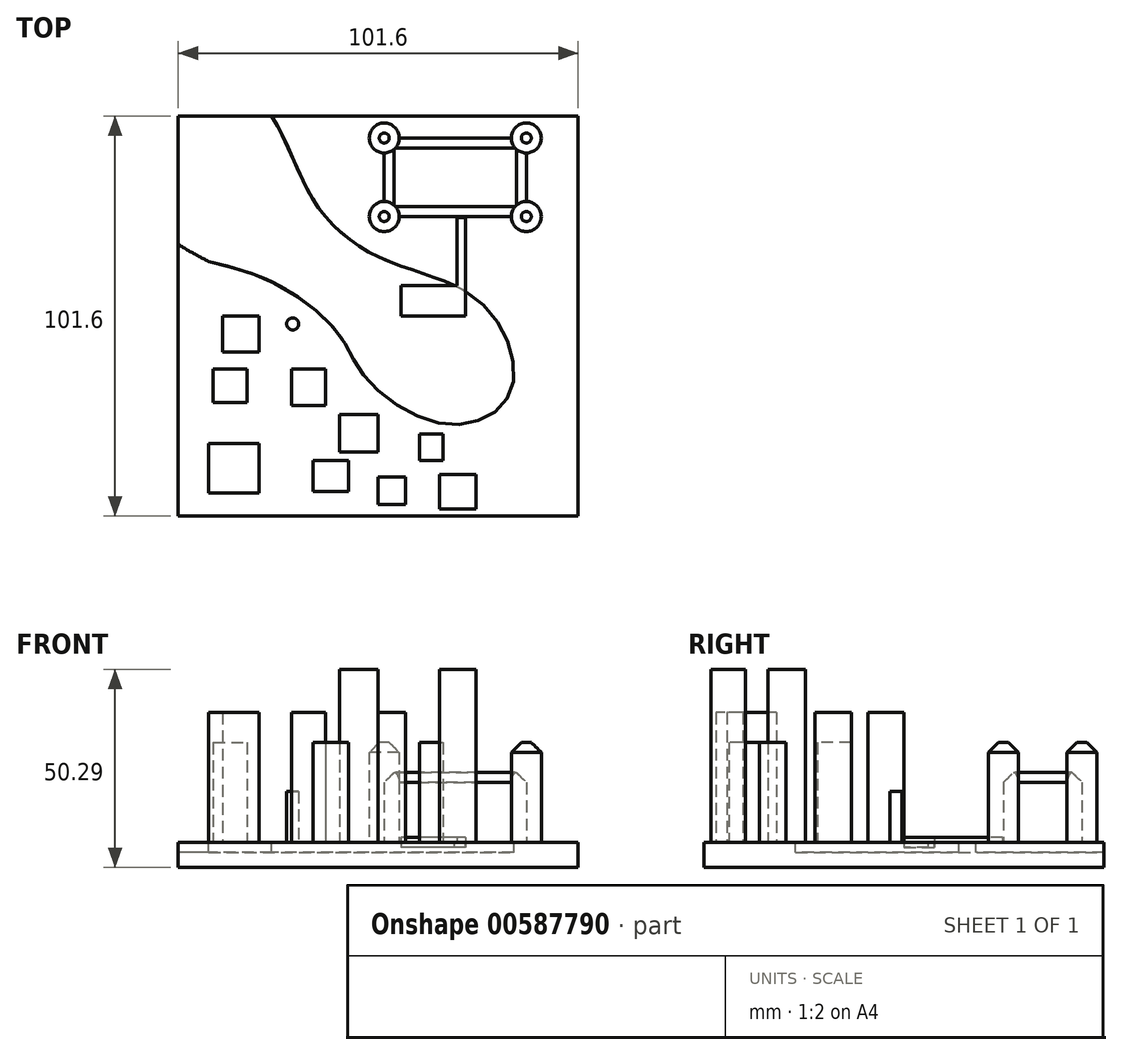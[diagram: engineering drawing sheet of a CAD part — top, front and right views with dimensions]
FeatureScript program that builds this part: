
annotation { "Feature Type Name" : "Feature", "Feature Type Description" : "" }
export const myFeature = defineFeature(function(context is Context, id is Id, definition is map)
    precondition{}
    {
        {
            var Q0;
            Q0=qCreatedBy(makeId("Top.planeOp"),FACE);
            var sketch = newSketch(context, id + "F0", { "sketchPlane" : qUnion([Q0])});
            skLineSegment(sketch, "E0.bottom", {"start": v(-50.8, -50.8) * mm, "end": v(50.8, -50.8) * mm});
            skLineSegment(sketch, "E0.top", {"start": v(-50.8, 50.8) * mm, "end": v(50.8, 50.8) * mm});
            skLineSegment(sketch, "E0.left", {"start": v(-50.8, -50.8) * mm, "end": v(-50.8, 50.8) * mm});
            skLineSegment(sketch, "E0.right", {"start": v(50.8, -50.8) * mm, "end": v(50.8, 50.8) * mm});
            skPoint(sketch, "E0.middle", {"position": v(0, 0) * mm});
            skSolve(sketch);
        }
        {
            var Q0;
            Q0 = qSketchRegion(id + "F0", true);
            extrude(context, id + "F1", {"entities" : qUnion([Q0]), "oppositeDirection" : true, "depth" : 6.35 * mm, "offsetDistance" : 25.4 * mm});
        }
        {
            var Q0;
            Q0=qCreatedBy(makeId("Top.planeOp"),FACE);
            var sketch = newSketch(context, id + "F2", { "sketchPlane" : qUnion([Q0])});
            skFitSpline(sketch, "E1", {"points": [v(-43.1, 13.89) * mm, v(-25.52, 7.95) * mm, v(-9.85, -4.87) * mm, v(-3.68, -15.08) * mm, v(10.8, -25.76) * mm, v(25.05, -26.7) * mm, v(33.6, -19.35) * mm, v(32.65, -5.82) * mm, v(21.72, 6.53) * mm, v(0, 15.08) * mm, v(-16.5, 29.56) * mm, v(-26.95, 50.69) * mm, v(-40.6, 65.37) * mm], "startDerivative": vector(201.87, -49.36) * mm, "endDerivative": vector(-139.7, 111.84) * mm});
            skFitSpline(sketch, "E2", {"points": [v(-43.1, 13.89) * mm, v(-58.29, 25.05) * mm, v(-64.82, 45.42) * mm], "startDerivative": vector(-35.32, 18.48) * mm, "endDerivative": vector(-0.32, 35.88) * mm});
            skLineSegment(sketch, "E3", {"start": v(-40.6, 65.37) * mm, "end": v(-64.82, 45.42) * mm});
            skSolve(sketch);
        }
        {
            var Q0;
            Q0 = qSketchRegion(id + "F2", true);
            extrude(context, id + "F3", {"entities" : qUnion([Q0]), "operationType" : NewBodyOperationType.REMOVE, "oppositeDirection" : true, "depth" : 2.54 * mm, "offsetDistance" : 25.4 * mm});
        }
        {
            var Q0;
            Q0=qCreatedBy(makeId("Top.planeOp"),FACE);
            var sketch = newSketch(context, id + "F4", { "sketchPlane" : qUnion([Q0])});
            skLineSegment(sketch, "E4.bottom", {"start": v(-41.9, -13.41) * mm, "end": v(-33.36, -13.41) * mm});
            skLineSegment(sketch, "E4.top", {"start": v(-41.9, -21.96) * mm, "end": v(-33.36, -21.96) * mm});
            skLineSegment(sketch, "E4.left", {"start": v(-41.9, -13.41) * mm, "end": v(-41.9, -21.96) * mm});
            skLineSegment(sketch, "E4.right", {"start": v(-33.36, -13.41) * mm, "end": v(-33.36, -21.96) * mm});
            skLineSegment(sketch, "E5.bottom", {"start": v(-16.5, -36.68) * mm, "end": v(-7.48, -36.68) * mm});
            skLineSegment(sketch, "E5.top", {"start": v(-16.5, -44.52) * mm, "end": v(-7.48, -44.52) * mm});
            skLineSegment(sketch, "E5.left", {"start": v(-16.5, -36.68) * mm, "end": v(-16.5, -44.52) * mm});
            skLineSegment(sketch, "E5.right", {"start": v(-7.48, -36.68) * mm, "end": v(-7.48, -44.52) * mm});
            skLineSegment(sketch, "E6.bottom", {"start": v(10.57, -30.03) * mm, "end": v(16.5, -30.03) * mm});
            skLineSegment(sketch, "E6.top", {"start": v(10.57, -36.68) * mm, "end": v(16.5, -36.68) * mm});
            skLineSegment(sketch, "E6.left", {"start": v(10.57, -30.03) * mm, "end": v(10.57, -36.68) * mm});
            skLineSegment(sketch, "E6.right", {"start": v(16.5, -30.03) * mm, "end": v(16.5, -36.68) * mm});
            skSolve(sketch);
        }
        {
            var Q0;
            Q0=qCreatedBy(makeId("Top.planeOp"),FACE);
            var sketch = newSketch(context, id + "F5", { "sketchPlane" : qUnion([Q0])});
            skLineSegment(sketch, "E7.bottom", {"start": v(-39.53, 0) * mm, "end": v(-30.27, 0) * mm});
            skLineSegment(sketch, "E7.top", {"start": v(-39.53, -9.14) * mm, "end": v(-30.27, -9.14) * mm});
            skLineSegment(sketch, "E7.left", {"start": v(-39.53, 0) * mm, "end": v(-39.53, -9.14) * mm});
            skLineSegment(sketch, "E7.right", {"start": v(-30.27, 0) * mm, "end": v(-30.27, -9.14) * mm});
            skLineSegment(sketch, "E8.bottom", {"start": v(-21.96, -13.41) * mm, "end": v(-13.41, -13.41) * mm});
            skLineSegment(sketch, "E8.top", {"start": v(-21.96, -22.67) * mm, "end": v(-13.41, -22.67) * mm});
            skLineSegment(sketch, "E8.left", {"start": v(-21.96, -13.41) * mm, "end": v(-21.96, -22.67) * mm});
            skLineSegment(sketch, "E8.right", {"start": v(-13.41, -13.41) * mm, "end": v(-13.41, -22.67) * mm});
            skLineSegment(sketch, "E9.bottom", {"start": v(-30.27, -32.4) * mm, "end": v(-43.1, -32.4) * mm});
            skLineSegment(sketch, "E9.top", {"start": v(-30.27, -45) * mm, "end": v(-43.1, -45) * mm});
            skLineSegment(sketch, "E9.left", {"start": v(-30.27, -32.4) * mm, "end": v(-30.27, -45) * mm});
            skLineSegment(sketch, "E9.right", {"start": v(-43.1, -32.4) * mm, "end": v(-43.1, -45) * mm});
            skLineSegment(sketch, "E10.bottom", {"start": v(0, -40.95) * mm, "end": v(7, -40.95) * mm});
            skLineSegment(sketch, "E10.top", {"start": v(0, -47.84) * mm, "end": v(7, -47.84) * mm});
            skLineSegment(sketch, "E10.left", {"start": v(0, -40.95) * mm, "end": v(0, -47.84) * mm});
            skLineSegment(sketch, "E10.right", {"start": v(7, -40.95) * mm, "end": v(7, -47.84) * mm});
            skSolve(sketch);
        }
        {
            var Q0;
            Q0=qCreatedBy(makeId("Top.planeOp"),FACE);
            var sketch = newSketch(context, id + "F6", { "sketchPlane" : qUnion([Q0])});
            skLineSegment(sketch, "E11.bottom", {"start": v(-9.85, -25.05) * mm, "end": v(0, -25.05) * mm});
            skLineSegment(sketch, "E11.top", {"start": v(-9.85, -34.54) * mm, "end": v(0, -34.54) * mm});
            skLineSegment(sketch, "E11.left", {"start": v(-9.85, -25.05) * mm, "end": v(-9.85, -34.54) * mm});
            skLineSegment(sketch, "E11.right", {"start": v(0, -25.05) * mm, "end": v(0, -34.54) * mm});
            skLineSegment(sketch, "E12.bottom", {"start": v(15.55, -40.24) * mm, "end": v(24.81, -40.24) * mm});
            skLineSegment(sketch, "E12.top", {"start": v(15.55, -49.03) * mm, "end": v(24.81, -49.03) * mm});
            skLineSegment(sketch, "E12.left", {"start": v(15.55, -40.24) * mm, "end": v(15.55, -49.03) * mm});
            skLineSegment(sketch, "E12.right", {"start": v(24.81, -40.24) * mm, "end": v(24.81, -49.03) * mm});
            skSolve(sketch);
        }
        {
            var Q0;
            Q0=qCreatedBy(makeId("Top.planeOp"),FACE);
            var sketch = newSketch(context, id + "F7", { "sketchPlane" : qUnion([Q0])});
            skCircle(sketch, "E13", {"center": v(-21.72, -2.02) * mm, "radius": 1.52 * mm});
            skSolve(sketch);
        }
        {
            var Q0;
            Q0=qCreatedBy(makeId("Top.planeOp"),FACE);
            var sketch = newSketch(context, id + "F8", { "sketchPlane" : qUnion([Q0])});
            skLineSegment(sketch, "E14.bottom", {"start": v(37.63, 25.29) * mm, "end": v(1.54, 25.29) * mm});
            skLineSegment(sketch, "E14.top", {"start": v(37.63, 45.23) * mm, "end": v(1.54, 45.23) * mm});
            skLineSegment(sketch, "E14.left", {"start": v(37.63, 25.29) * mm, "end": v(37.63, 45.23) * mm});
            skLineSegment(sketch, "E14.right", {"start": v(1.54, 25.29) * mm, "end": v(1.54, 45.23) * mm});
            skPoint(sketch, "E14.middle", {"position": v(19.59, 35.26) * mm});
            skSolve(sketch);
        }
        {
            var Q0;
            Q0=qCreatedBy(makeId("Top.planeOp"),FACE);
            var sketch = newSketch(context, id + "F9", { "sketchPlane" : qUnion([Q0])});
            skLineSegment(sketch, "E15.bottom", {"start": v(22.2, 25.05) * mm, "end": v(20.06, 25.05) * mm});
            skLineSegment(sketch, "E15.top", {"start": v(22.2, 0) * mm, "end": v(20.06, 0) * mm});
            skLineSegment(sketch, "E15.left", {"start": v(22.2, 25.05) * mm, "end": v(22.2, 0) * mm});
            skLineSegment(sketch, "E15.right", {"start": v(20.06, 25.05) * mm, "end": v(20.06, 0) * mm});
            skLineSegment(sketch, "E16.bottom", {"start": v(20.06, 0) * mm, "end": v(5.82, 0) * mm});
            skLineSegment(sketch, "E16.top", {"start": v(20.06, 7.72) * mm, "end": v(5.82, 7.72) * mm});
            skLineSegment(sketch, "E16.left", {"start": v(20.06, 0) * mm, "end": v(20.06, 7.72) * mm});
            skLineSegment(sketch, "E16.right", {"start": v(5.82, 0) * mm, "end": v(5.82, 7.72) * mm});
            skSolve(sketch);
        }
        {
            var Q0;
            Q0 = qSketchRegion(id + "F4", true);
            extrude(context, id + "F10", {"entities" : qUnion([Q0]), "operationType" : NewBodyOperationType.ADD, "depth" : 25.4 * mm, "offsetDistance" : 25.4 * mm});
        }
        {
            var Q0;
            Q0 = qSketchRegion(id + "F5", true);
            extrude(context, id + "F11", {"entities" : qUnion([Q0]), "operationType" : NewBodyOperationType.ADD, "depth" : 33.02 * mm, "offsetDistance" : 25.4 * mm});
        }
        {
            var Q0;
            Q0 = qSketchRegion(id + "F6", true);
            extrude(context, id + "F12", {"entities" : qUnion([Q0]), "operationType" : NewBodyOperationType.ADD, "depth" : 43.94 * mm, "offsetDistance" : 25.4 * mm});
        }
        {
            var Q0;
            Q0 = qSketchRegion(id + "F7", true);
            extrude(context, id + "F13", {"entities" : qUnion([Q0]), "operationType" : NewBodyOperationType.ADD, "depth" : 12.95 * mm, "offsetDistance" : 25.4 * mm});
        }
        {
            var Q0;
            Q0 = qSketchRegion(id + "F8", true);
            extrude(context, id + "F14", {"entities" : qUnion([Q0]), "operationType" : NewBodyOperationType.ADD, "depth" : 17.78 * mm, "offsetDistance" : 25.4 * mm});
        }
        {
            var Q0;
            Q0=qCreatedBy(makeId("Top.planeOp"),FACE);
            var sketch = newSketch(context, id + "F15", { "sketchPlane" : qUnion([Q0])});
            skCircle(sketch, "E17", {"center": v(1.54, 45.23) * mm, "radius": 3.81 * mm});
            skCircle(sketch, "E18", {"center": v(37.63, 45.23) * mm, "radius": 3.81 * mm});
            skCircle(sketch, "E19", {"center": v(37.63, 25.29) * mm, "radius": 3.81 * mm});
            skCircle(sketch, "E20", {"center": v(1.54, 25.29) * mm, "radius": 3.81 * mm});
            skSolve(sketch);
        }
        {
            var Q0;
            Q0 = qSketchRegion(id + "F15", true);
            extrude(context, id + "F16", {"entities" : qUnion([Q0]), "operationType" : NewBodyOperationType.ADD, "depth" : 25.4 * mm, "offsetDistance" : 25.4 * mm});
        }
        {
            var Q0;
            Q0=makeQuery(id+"F16.opExtrude","CAP_EDGE",EDGE,{"disambiguationData":[OSD([sQuery(id+"F15.wireOp",EDGE,"E17")])],"isStart":false});
            var Q1;
            Q1=makeQuery(id+"F16.opExtrude","CAP_EDGE",EDGE,{"disambiguationData":[OSD([sQuery(id+"F15.wireOp",EDGE,"E20")])],"isStart":false});
            var Q2;
            Q2=makeQuery(id+"F16.opExtrude","CAP_EDGE",EDGE,{"disambiguationData":[OSD([sQuery(id+"F15.wireOp",EDGE,"E19")])],"isStart":false});
            var Q3;
            Q3=makeQuery(id+"F16.opExtrude","CAP_EDGE",EDGE,{"disambiguationData":[OSD([sQuery(id+"F15.wireOp",EDGE,"E18")])],"isStart":false});
            chamfer(context, id + "F17", {"entities" : qUnion([Q0, Q1, Q2, Q3]), "width" : 2.54 * mm, "tangentPropagation" : true});
        }
        {
            var Q0;
            Q0=makeQuery(id+"F14.opExtrude","CAP_EDGE",EDGE,{"disambiguationData":[OSD([sQuery(id+"F8.wireOp",EDGE,"E14.right")])],"isStart":false});
            var Q1;
            Q1=makeQuery(id+"F14.opExtrude","CAP_EDGE",EDGE,{"disambiguationData":[OSD([sQuery(id+"F8.wireOp",EDGE,"E14.bottom")])],"isStart":false});
            var Q2;
            Q2=makeQuery(id+"F14.opExtrude","CAP_EDGE",EDGE,{"disambiguationData":[OSD([sQuery(id+"F8.wireOp",EDGE,"E14.left")])],"isStart":false});
            var Q3;
            Q3=makeQuery(id+"F14.opExtrude","CAP_EDGE",EDGE,{"disambiguationData":[OSD([sQuery(id+"F8.wireOp",EDGE,"E14.top")])],"isStart":false});
            chamfer(context, id + "F18", {"entities" : qUnion([Q0, Q1, Q2, Q3]), "width" : 2.54 * mm, "tangentPropagation" : true});
        }
        {
            var Q0;
            Q0 = qSketchRegion(id + "F9", true);
            extrude(context, id + "F19", {"entities" : qUnion([Q0]), "operationType" : NewBodyOperationType.ADD, "endBound" : BoundingType.SYMMETRIC, "depth" : 2.54 * mm, "offsetDistance" : 25.4 * mm});
        }
    });
